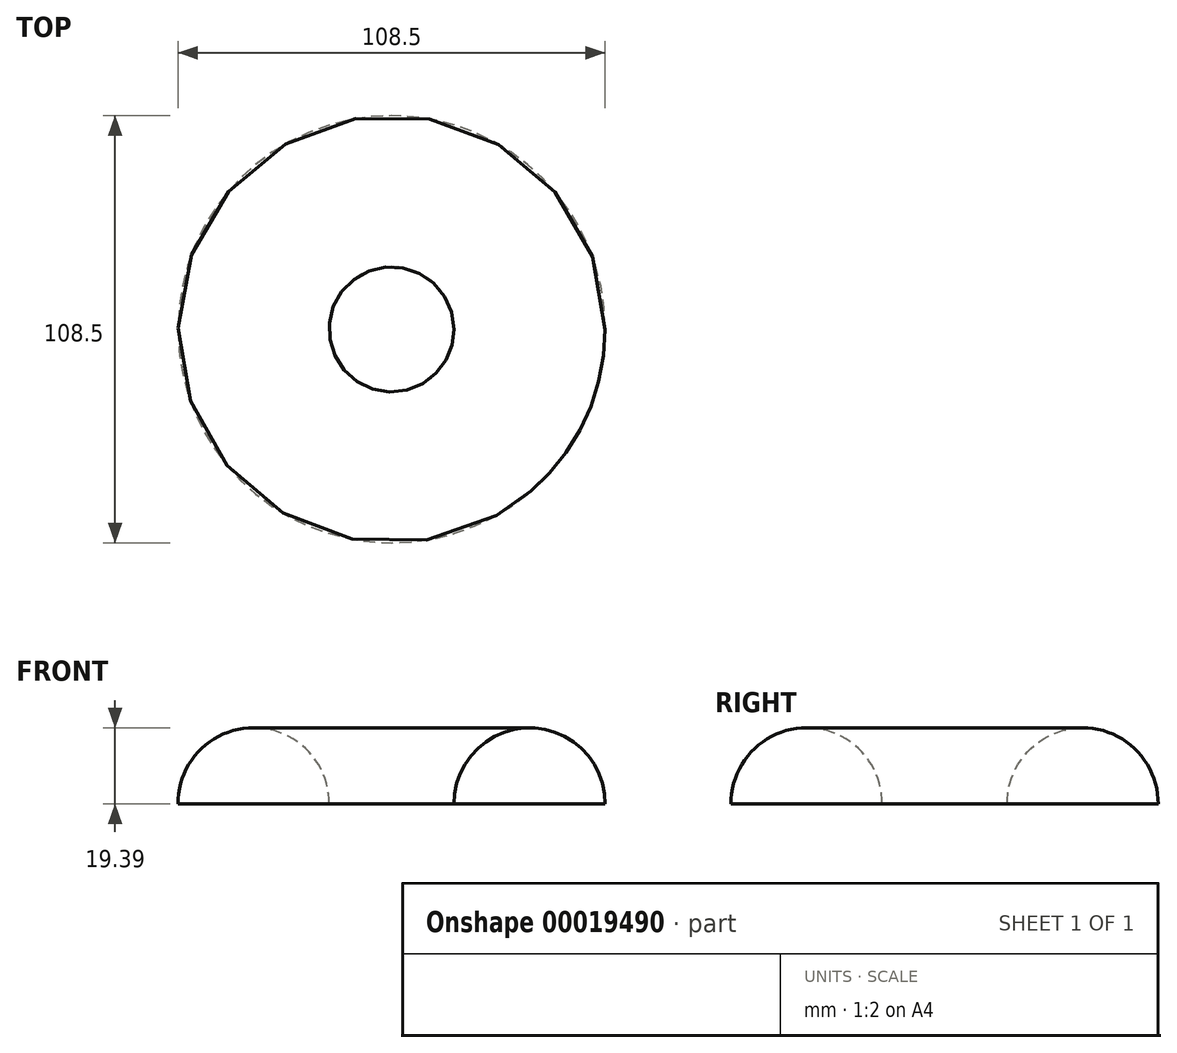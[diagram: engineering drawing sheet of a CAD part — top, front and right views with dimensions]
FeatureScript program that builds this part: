
annotation { "Feature Type Name" : "Feature", "Feature Type Description" : "" }
export const myFeature = defineFeature(function(context is Context, id is Id, definition is map)
    precondition{}
    {
        {
            var Q0;
            Q0=qCreatedBy(makeId("Front.planeOp"),FACE);
            var sketch = newSketch(context, id + "F0", { "sketchPlane" : qUnion([Q0])});
            skArc(sketch, "E0", {"start": v(54.25, 0) * mm, "mid": v(35.07, 19.39) * mm, "end": v(15.89, 0) * mm});
            skLineSegment(sketch, "E1", {"start": v(15.89, 0) * mm, "end": v(54.25, 0) * mm});
            skLineSegment(sketch, "E2", {"start": v(0, 0) * mm, "end": v(0, 42.1) * mm, "construction": true});
            skSolve(sketch);
        }
        {
            var Q0;
            Q0 = qConstructionFilter(qBodyType(qCreatedBy(id + "F0" ,EDGE), BodyType.WIRE), ConstructionObject.NO);
            var Q1;
            Q1=sQuery(id+"F0.wireOp",EDGE,"E2");
            revolve(context, id + "F1", {"bodyType" : ToolBodyType.SURFACE, "surfaceEntities" : qUnion([Q0]), "axis" : qUnion([Q1]), "revolveType" : RevolveType.FULL});
        }
    });
